# Revit family: QF_BOURGEAT_Satellite4G_chaud_2-1_vitree_ouverture_gauche
name_source: partatom
category: Equipement spécialisé
revit_build: Autodesk Revit 2015 (Build: 20140606_1530(x64)
units: mm (PartAtom-declared; Revit-internal decimal feet)

## types (6) — shared parameters
Certification = NF hygiene alimentaire
Diametre_roue = 160 mm  [stored 0.524934 ft]
Fabricant = BOURGEAT
Fréquence = 50 Hz
Hauteur_roue = 200 mm  [stored 0.656168 ft]
Indice de protection = IP25
Largeur_porte = 706 mm  [stored 2.31627 ft]
Longueur hors tout = 791 mm
Longueur_poignees_laterales = 803 mm  [stored 2.63451 ft]
Materiau_Poignee_porte = B_Elastomère_TPE_S
Materiau_bac = B_Elastomère_TPE_S
Materiau_bandage = B_Elastomère_TPE_S
Materiau_porte = Acier inoxydable, brossé
Materiau_vitre = Verre, vitrage transparent, trempé
Materiaux_reserve_eau = Acrylique, transparent
Nature isolant = Mousse sans PU
Phase = 2
Poignee_droite = Non
Poignee_gauche = Oui
Pos_IHM_bord_gauche_porte_gauche = 175 mm  [stored 0.574147 ft]
Pos_V_IHM = 98 mm  [stored 0.321522 ft]
Pos_vitre_bord_gauche_porte_gauche = 350 mm  [stored 1.14829 ft]
Profondeur hors tout = 959 mm  [stored 3.14633 ft]
Spécification du Fabricant = Satellite 4G
Tension = 230 V
URL catalogue = http://www.bourgeat.fr

## per-type parameters (varying)
| type | Charge max | Consommation énergétique | Hauteur hors tout | Hauteur_poignee_porte_sol | Hauteur_poignees_laterales | Hauteur_porte | Humidification | Intensité nominale | Modèle | Poids net à vide | Puissance électrique  |
| GN40_humidification_tirant_gauche | 300.00 kg | 1.52 Kwh/h NFD40-016 | 1876 mm | 816 mm | 906 mm  [stored 2.97244 ft] | 1629 mm  [stored 5.34449 ft] | Oui | 13 A | 841340 | 140.00 kg | 2950 W |
| GN30_humidification_tirant_gauche | 2500.00 kg | 1.2 Kwh/h NFD40-016 | 1521 mm  [stored 4.99016 ft] | 564 mm | 906 mm  [stored 2.97244 ft] | 1274 mm  [stored 4.17979 ft] | Oui | 10 A | 841330 | 1200.00 kg | 2350 W |
| GN20_humidification_tirant_gauche | 200.00 kg | 0.8 Kwh/h NFD40-016 | 1166 mm | 477 mm  [stored 1.56496 ft] | 806 mm  [stored 2.64436 ft] | 919 mm | Oui | 8 A | 841320 | 100.00 kg | 1750 W |
| GN20_sans_humidification_tirant_gauche | 200.00 kg | 0.8 Kwh/h NFD40-016 | 1166 mm | 477 mm  [stored 1.56496 ft] | 806 mm  [stored 2.64436 ft] | 919 mm | Non | 8 A | 841220 | 100.00 kg | 1750 W |
| GN30_sans_humidification_tirant_gauche | 250.00 kg | 1.2 Kwh/h NFD40-016 | 1521 mm  [stored 4.99016 ft] | 564 mm | 906 mm  [stored 2.97244 ft] | 1274 mm  [stored 4.17979 ft] | Non | 10 A | 841230 | 120.00 kg | 2350 W |
| GN40_sans_humidification_tirant_gauche | 300.00 kg | 1.52 Kwh/h NFD40-016 | 1876 mm | 816 mm | 906 mm  [stored 2.97244 ft] | 1629 mm  [stored 5.34449 ft] | Non | 13 A | 841240 | 140.00 kg | 2950 W |

note: [stored X ft] marks values corroborated as IEEE doubles in the binary element streams (Revit-internal decimal feet)
